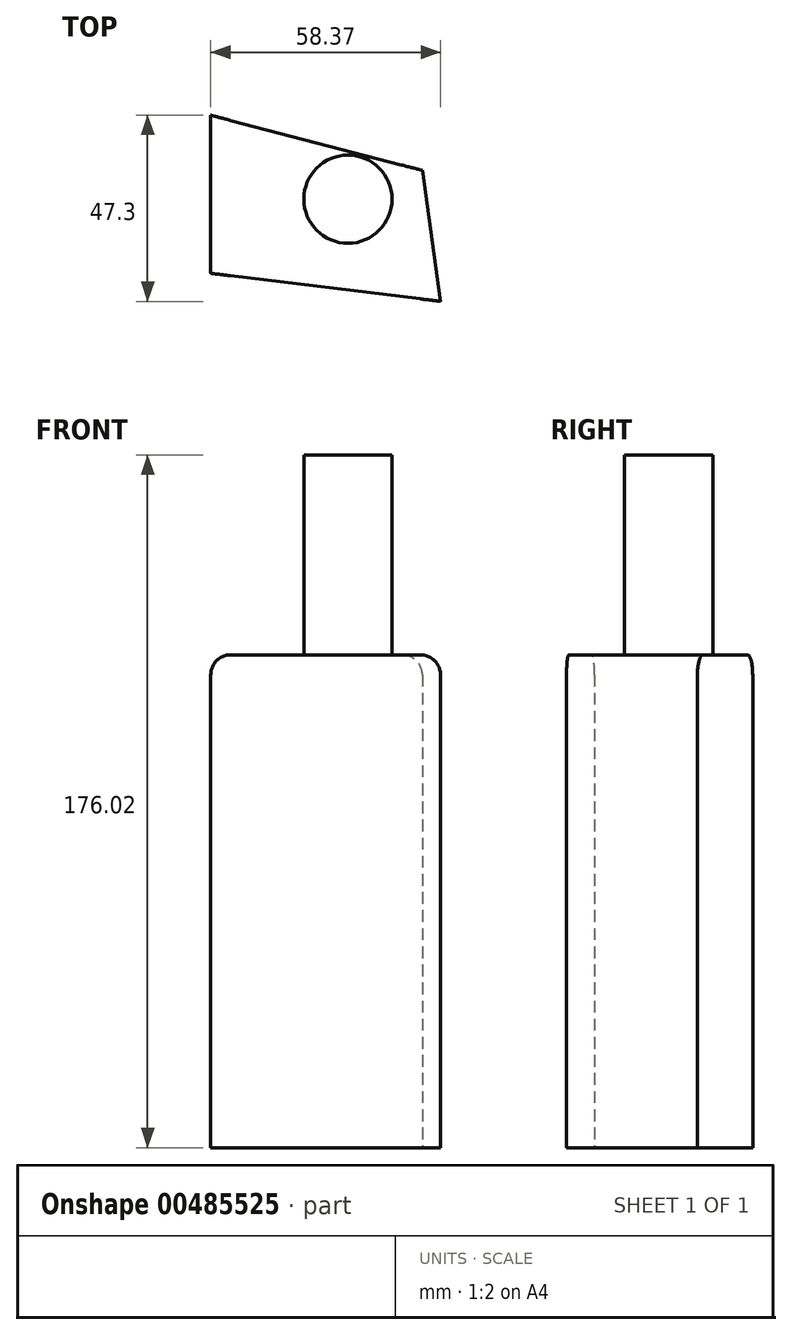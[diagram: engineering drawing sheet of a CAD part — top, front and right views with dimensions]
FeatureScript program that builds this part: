
annotation { "Feature Type Name" : "Feature", "Feature Type Description" : "" }
export const myFeature = defineFeature(function(context is Context, id is Id, definition is map)
    precondition{}
    {
        {
            var Q0;
            Q0=qCreatedBy(makeId("Top.planeOp"),FACE);
            var sketch = newSketch(context, id + "F0", { "sketchPlane" : qUnion([Q0])});
            skLineSegment(sketch, "E0", {"start": v(-28.97, 33.82) * mm, "end": v(-28.97, -6.35) * mm});
            skLineSegment(sketch, "E1", {"start": v(-28.97, -6.35) * mm, "end": v(29.4, -13.48) * mm});
            skLineSegment(sketch, "E2", {"start": v(29.4, -13.48) * mm, "end": v(24.8, 19.8) * mm});
            skLineSegment(sketch, "E3", {"start": v(24.8, 19.8) * mm, "end": v(-28.97, 33.82) * mm});
            skSolve(sketch);
        }
        {
            var Q0;
            Q0 = qSketchRegion(id + "F0", true);
            extrude(context, id + "F1", {"entities" : qUnion([Q0]), "depth" : 125.22 * mm});
        }
        {
            var Q0;
            Q0=makeQuery(id+"F1.opExtrude","CAP_EDGE",EDGE,{"disambiguationData":[OSD([sQuery(id+"F0.wireOp",EDGE,"E2")])],"isStart":false});
            fillet(context, id + "F2", {"entities" : qUnion([Q0]), "radius" : 5.08 * mm, "tangentPropagation" : true, "allowEdgeOverflow" : false});
        }
        {
            var Q0;
            Q0=makeQuery(id+"F1.opExtrude","CAP_EDGE",EDGE,{"disambiguationData":[OSD([sQuery(id+"F0.wireOp",EDGE,"E0")])],"isStart":false});
            fillet(context, id + "F3", {"entities" : qUnion([Q0]), "radius" : 5.08 * mm, "tangentPropagation" : true, "allowEdgeOverflow" : false});
        }
        {
            var Q0;
            Q0=makeQuery(id+"F1.opExtrude","CAP_FACE",FACE,{"disambiguationData":[OSD([sQuery(id+"F0.wireOp",EDGE,"E0"),sQuery(id+"F0.wireOp",EDGE,"E1"),sQuery(id+"F0.wireOp",EDGE,"E2"),sQuery(id+"F0.wireOp",EDGE,"E3")])],"isStart":false});
            var sketch = newSketch(context, id + "F4", { "sketchPlane" : qUnion([Q0])});
            skCircle(sketch, "E4", {"center": v(5.88, 12.49) * mm, "radius": 11.21 * mm});
            skSolve(sketch);
        }
        {
            var Q0;
            Q0 = qSketchRegion(id + "F4", true);
            extrude(context, id + "F5", {"entities" : qUnion([Q0]), "operationType" : NewBodyOperationType.ADD, "depth" : 50.8 * mm});
        }
    });
